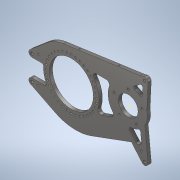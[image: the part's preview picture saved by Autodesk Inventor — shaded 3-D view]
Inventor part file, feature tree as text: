
AUTODESK INVENTOR PART (.ipt)
format: ipt  version: 2021 (Build 250183000, 183)  size: 533,504 bytes
history: native  units: in
note: dims shown in document units (in); Inventor stores cm internally (conversion verified against a paired STEP export)
features: sketch x16, extrude x12, fillet x7, hole x5, chamfer x1, projected_geometry x1
ambient origin geometry x8: Origin, YZ Plane, XZ Plane, XY Plane, X Axis, Y Axis, Z Axis, Center Point
bodies: Body1 (feature_tree)
feature tree (42):
  extrude  "Extrusion13"  Depth=0.5in TaperAngle=0.0deg
  hole  "Hole4"  [1 undecoded]
  extrude  "Extrusion15"  Depth=1.0in
  extrude  "Extrusion17"  Depth=0.5in TaperAngle=0.0deg
  hole  "Hole9"  [1 undecoded]
  hole  "Hole10"  [1 undecoded]
  extrude  "Extrusion18"  Depth=1.0in
  extrude  "Extrusion19"  Depth=0.239in
  extrude  "Extrusion24"  Depth=0.5in
  fillet  "Fillet3"  Radius=0.1718in
  extrude  "Extrusion27"  Depth=0.75in
  chamfer  "Chamfer1"  Distance=1.0in
  sketch  "Sketch40"  dims[d194=0.3526in d197=0.239in]
  extrude  "Extrusion29"  Depth=0.25in
  extrude  "Extrusion30"  Depth=0.5in TaperAngle=0.0deg
  fillet  "Fillet4"  Radius=0.75in
  fillet  "Fillet5"  Radius=1.0in
  extrude  "Extrusion32"  Depth=0.75in
  extrude  "Extrusion35"  Depth=0.75in
  fillet  "Fillet6"  Radius=0.5in
  fillet  "Fillet7"  Radius=2.8in
  extrude  "Extrusion36"  Depth=0.25in
  fillet  "Fillet8"  Radius=0.5in
  hole  "Hole12"  [1 undecoded]
  hole  "Hole14"  [1 undecoded]
  fillet  "Fillet9"  Radius=1.0in
  sketch  "Sketch14"  dims[d96=8.5in d97=2.16in d98=9.0in d99=5.5in d100=1.0in d101=1.0in d102=6.0in d103=6.0in d104=3.718in d105=1.0in d108=10.718in d109=1.5in d111=0.5in d112=0.0in]
  sketch  "Sketch15"  dims[d113=0.386in d114=0.75in d115=0.762in d116=0.25in d117=0.5635in d118=0.484in d119=0.8108in d132=5.0in]
  sketch  "Sketch18"  dims[d133=17.223in d134=1.0in]
  sketch  "Sketch21"  dims[d135=1.0in d136=0.5in d137=0.0in]
  sketch  "Sketch29"  dims[d155=1.0in d156=0.0in d178=7.75in]
  sketch  "Sketch31"  dims[d179=3.5433in d181=360.0deg]
  sketch  "Sketch32"  dims[d183=0.257in d184=0.75in d185=0.438in d186=0.25in d187=0.5635in d188=1.0in d189=0.8108in d191=1.0in]
  sketch  "Sketch39"  dims[d192=0.0481in d193=1.0in]
  sketch  "Sketch42"  dims[d198=0.1195in d199=0.5in]
  sketch  "Sketch43"  dims[d200=0.266in d201=0.75in d202=0.507in d203=0.25in d204=0.5635in d205=1.0in d206=0.8108in d207=0.1718in]
  sketch  "Sketch45"  dims[d208=15.0deg d210=0.75in]
  sketch  "Sketch48"  dims[d211=0.75in]
  sketch  "Sketch49"  dims[d212=0.75in]
  sketch  "Sketch51"  dims[d213=0.25in]
  sketch  "Sketch54"  dims[d214=0.5in d215=1.0in d216=0.0in d217=0.25in d218=1.0in d219=0.0in d223=0.75in d242=1.0in d243=0.0in d247=0.75in d249=0.75in d250=0.5in d251=2.8in d262=0.25in d263=0.5in d264=1.0in d265=0.0in d266=0.0156in d267=0.125in d268=45.0deg d284=1.0in d285=0.0in d296=6.75in d297=1.0in d298=0.0in d303=3.005in d304=8.715in d305=6.5in d306=0.5in d307=0.5in d308=4.44in d309=0.325in d310=1.9685in d312=360.0deg d314=1.0in d315=0.0in d317=0.061in d332=0.055in d333=0.5in d334=0.0in d335=11.5in d336=5.0in d337=3.0in d339=0.5in d340=0.0in d341=7.0in d353=2.25in d354=8.375in d355=0.25in d356=0.196in d357=0.5in d358=0.375in d359=0.25in d360=0.5635in d361=0.65in d362=0.8108in d370=0.25in d371=1.75in d372=0.196in d373=0.5in d374=0.375in d375=0.25in d376=0.5635in d377=0.65in d378=0.8108in d379=3.0in d381=6.4in d382=0.25in d383=0.0069in d283=0.5in d286=0.0344in]
  projected_geometry  "Project Cut Edges1"
note: 5 required parameter values undecoded (feature->parameter linkage not recoverable at this tier; creation-order binding heuristic only, values carry confidence <= 0.55)
